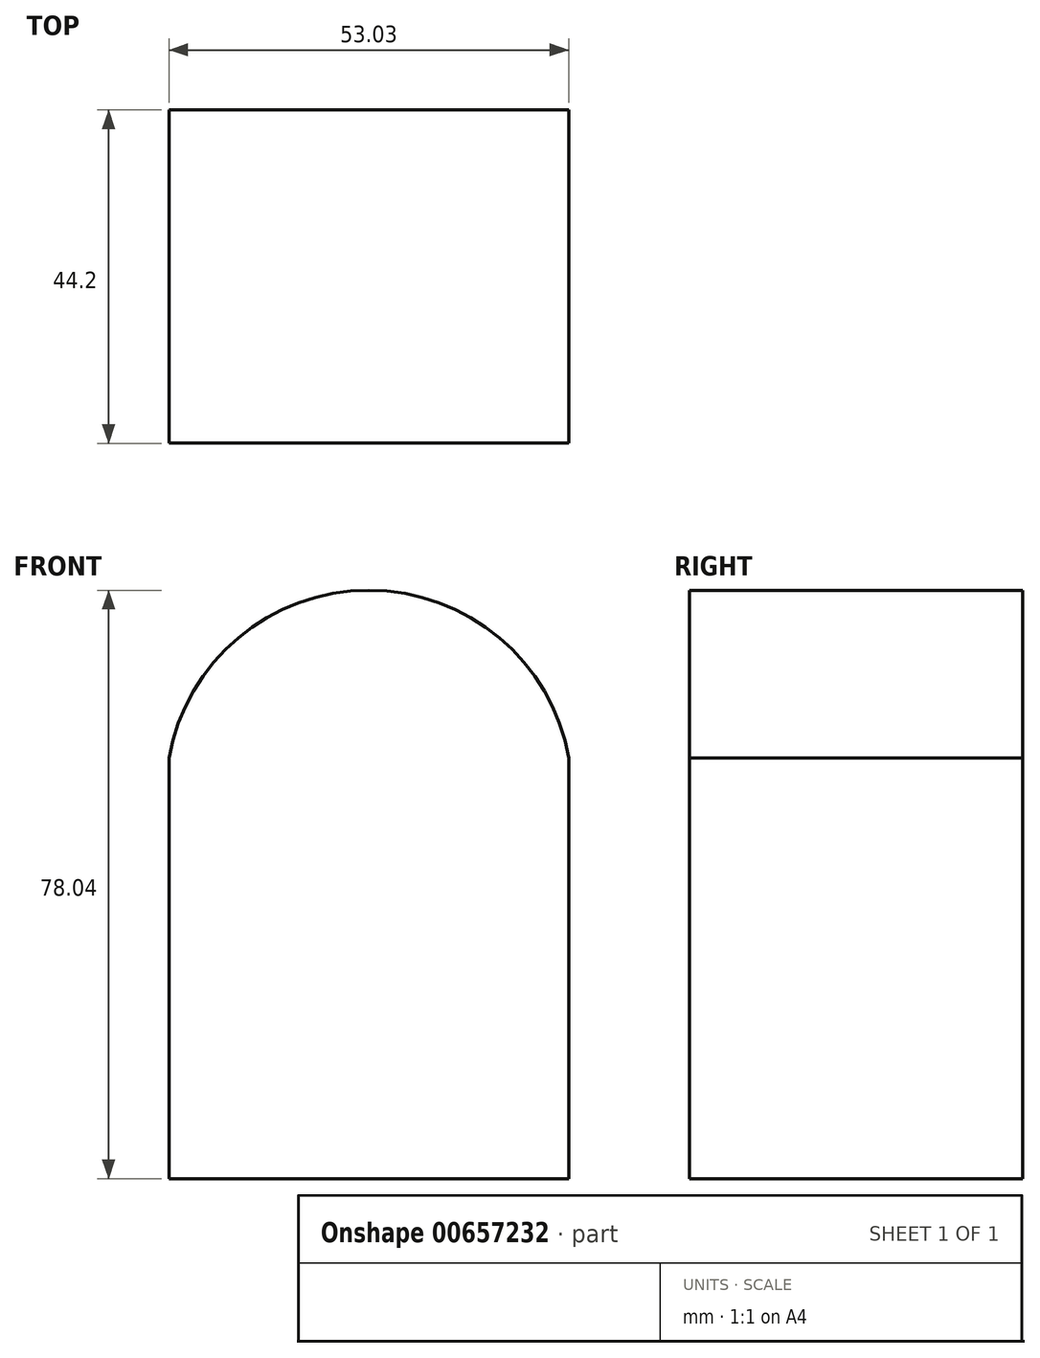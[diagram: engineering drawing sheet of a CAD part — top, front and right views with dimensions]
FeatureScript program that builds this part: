
annotation { "Feature Type Name" : "Feature", "Feature Type Description" : "" }
export const myFeature = defineFeature(function(context is Context, id is Id, definition is map)
    precondition{}
    {
        {
            var Q0;
            Q0=qCreatedBy(makeId("Front.planeOp"),FACE);
            var sketch = newSketch(context, id + "F0", { "sketchPlane" : qUnion([Q0])});
            skLineSegment(sketch, "E0.bottom", {"start": v(-24.84, 17.07) * mm, "end": v(28.2, 17.07) * mm});
            skLineSegment(sketch, "E0.top", {"start": v(-24.84, -38.7) * mm, "end": v(28.2, -38.7) * mm});
            skLineSegment(sketch, "E0.left", {"start": v(-24.84, 17.07) * mm, "end": v(-24.84, -38.7) * mm});
            skLineSegment(sketch, "E0.right", {"start": v(28.2, 17.07) * mm, "end": v(28.2, -38.7) * mm});
            skArc(sketch, "E1", {"start": v(28.2, 17.07) * mm, "mid": v(1.68, 39.33) * mm, "end": v(-24.84, 17.07) * mm});
            skSolve(sketch);
        }
        {
            var Q0;
            Q0 = qSketchRegion(id + "F0", true);
            extrude(context, id + "F1", {"entities" : qUnion([Q0]), "depth" : 44.2 * mm, "offsetDistance" : 25.4 * mm});
        }
    });
